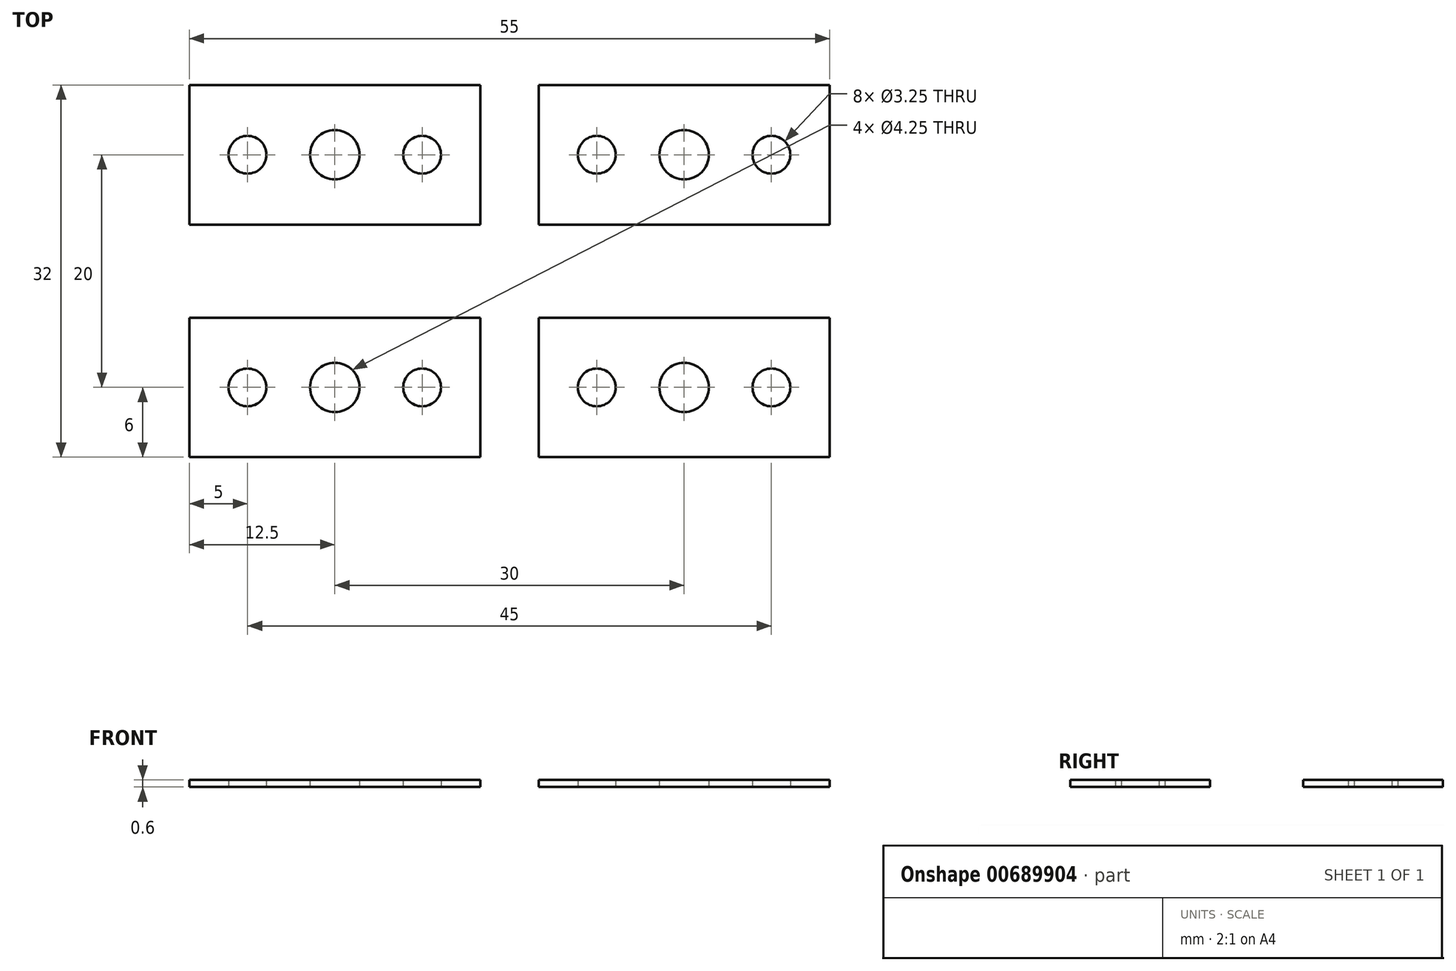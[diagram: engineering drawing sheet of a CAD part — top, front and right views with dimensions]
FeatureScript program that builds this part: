
annotation { "Feature Type Name" : "Feature", "Feature Type Description" : "" }
export const myFeature = defineFeature(function(context is Context, id is Id, definition is map)
    precondition{}
    {
        {
            var Q0;
            Q0=qCreatedBy(makeId("Top.planeOp"),FACE);
            var sketch = newSketch(context, id + "F0", { "sketchPlane" : qUnion([Q0])});
            skLineSegment(sketch, "E0.bottom", {"start": v(0, 0) * mm, "end": v(25, 0) * mm});
            skLineSegment(sketch, "E0.top", {"start": v(0, 12) * mm, "end": v(25, 12) * mm});
            skLineSegment(sketch, "E0.left", {"start": v(0, 0) * mm, "end": v(0, 12) * mm});
            skLineSegment(sketch, "E0.right", {"start": v(25, 0) * mm, "end": v(25, 12) * mm});
            skCircle(sketch, "E1", {"center": v(12.5, 6) * mm, "radius": 2.12 * mm});
            skCircle(sketch, "E2", {"center": v(5, 6) * mm, "radius": 1.63 * mm});
            skCircle(sketch, "E3", {"center": v(20, 6) * mm, "radius": 1.63 * mm});
            skLineSegment(sketch, "E4.0.1.0", {"start": v(25, 20) * mm, "end": v(25, 32) * mm});
            skLineSegment(sketch, "E4.0.1.1", {"start": v(0, 20) * mm, "end": v(25, 20) * mm});
            skCircle(sketch, "E4.0.1.2", {"center": v(12.5, 26) * mm, "radius": 2.12 * mm});
            skCircle(sketch, "E4.0.1.3", {"center": v(20, 26) * mm, "radius": 1.63 * mm});
            skCircle(sketch, "E4.0.1.4", {"center": v(5, 26) * mm, "radius": 1.63 * mm});
            skLineSegment(sketch, "E4.0.1.5", {"start": v(0, 20) * mm, "end": v(0, 32) * mm});
            skLineSegment(sketch, "E4.0.1.6", {"start": v(0, 32) * mm, "end": v(25, 32) * mm});
            skLineSegment(sketch, "E4.1.0.0", {"start": v(55, 0) * mm, "end": v(55, 12) * mm});
            skLineSegment(sketch, "E4.1.0.1", {"start": v(30, 0) * mm, "end": v(55, 0) * mm});
            skCircle(sketch, "E4.1.0.2", {"center": v(42.5, 6) * mm, "radius": 2.12 * mm});
            skCircle(sketch, "E4.1.0.3", {"center": v(50, 6) * mm, "radius": 1.63 * mm});
            skCircle(sketch, "E4.1.0.4", {"center": v(35, 6) * mm, "radius": 1.63 * mm});
            skLineSegment(sketch, "E4.1.0.5", {"start": v(30, 0) * mm, "end": v(30, 12) * mm});
            skLineSegment(sketch, "E4.1.0.6", {"start": v(30, 12) * mm, "end": v(55, 12) * mm});
            skLineSegment(sketch, "E4.1.1.0", {"start": v(55, 20) * mm, "end": v(55, 32) * mm});
            skLineSegment(sketch, "E4.1.1.1", {"start": v(30, 20) * mm, "end": v(55, 20) * mm});
            skCircle(sketch, "E4.1.1.2", {"center": v(42.5, 26) * mm, "radius": 2.12 * mm});
            skCircle(sketch, "E4.1.1.3", {"center": v(50, 26) * mm, "radius": 1.63 * mm});
            skCircle(sketch, "E4.1.1.4", {"center": v(35, 26) * mm, "radius": 1.63 * mm});
            skLineSegment(sketch, "E4.1.1.5", {"start": v(30, 20) * mm, "end": v(30, 32) * mm});
            skLineSegment(sketch, "E4.1.1.6", {"start": v(30, 32) * mm, "end": v(55, 32) * mm});
            skLineSegment(sketch, "E4.direction1", {"start": v(0, 0) * mm, "end": v(30, 0) * mm, "construction": true});
            skLineSegment(sketch, "E4.direction2", {"start": v(0, 0) * mm, "end": v(0, 20) * mm, "construction": true});
            skSolve(sketch);
        }
        {
            var Q0;
            Q0=makeQuery(id+"F0.imprint","IMPRINT",FACE,{"disambiguationData":[TD([[makeQuery(id+"F0.imprint","IMPRINT",EDGE,{"derivedFrom":sQuery(id+"F0.wireOp",EDGE,"E4.0.1.0")}),1.0]])]});
            var Q1;
            Q1=makeQuery(id+"F0.imprint","IMPRINT",FACE,{"disambiguationData":[TD([[makeQuery(id+"F0.imprint","IMPRINT",EDGE,{"derivedFrom":sQuery(id+"F0.wireOp",EDGE,"E4.1.1.0")}),1.0]])]});
            var Q2;
            Q2=makeQuery(id+"F0.imprint","IMPRINT",FACE,{"disambiguationData":[TD([[makeQuery(id+"F0.imprint","IMPRINT",EDGE,{"derivedFrom":sQuery(id+"F0.wireOp",EDGE,"E4.1.0.0")}),1.0]])]});
            var Q3;
            Q3=makeQuery(id+"F0.imprint","IMPRINT",FACE,{"disambiguationData":[TD([[makeQuery(id+"F0.imprint","IMPRINT",EDGE,{"derivedFrom":sQuery(id+"F0.wireOp",EDGE,"E0.bottom")}),1.0]])]});
            extrude(context, id + "F1", {"entities" : qUnion([Q0, Q1, Q2, Q3]), "depth" : 0.6 * mm, "offsetDistance" : 25 * mm});
        }
    });
